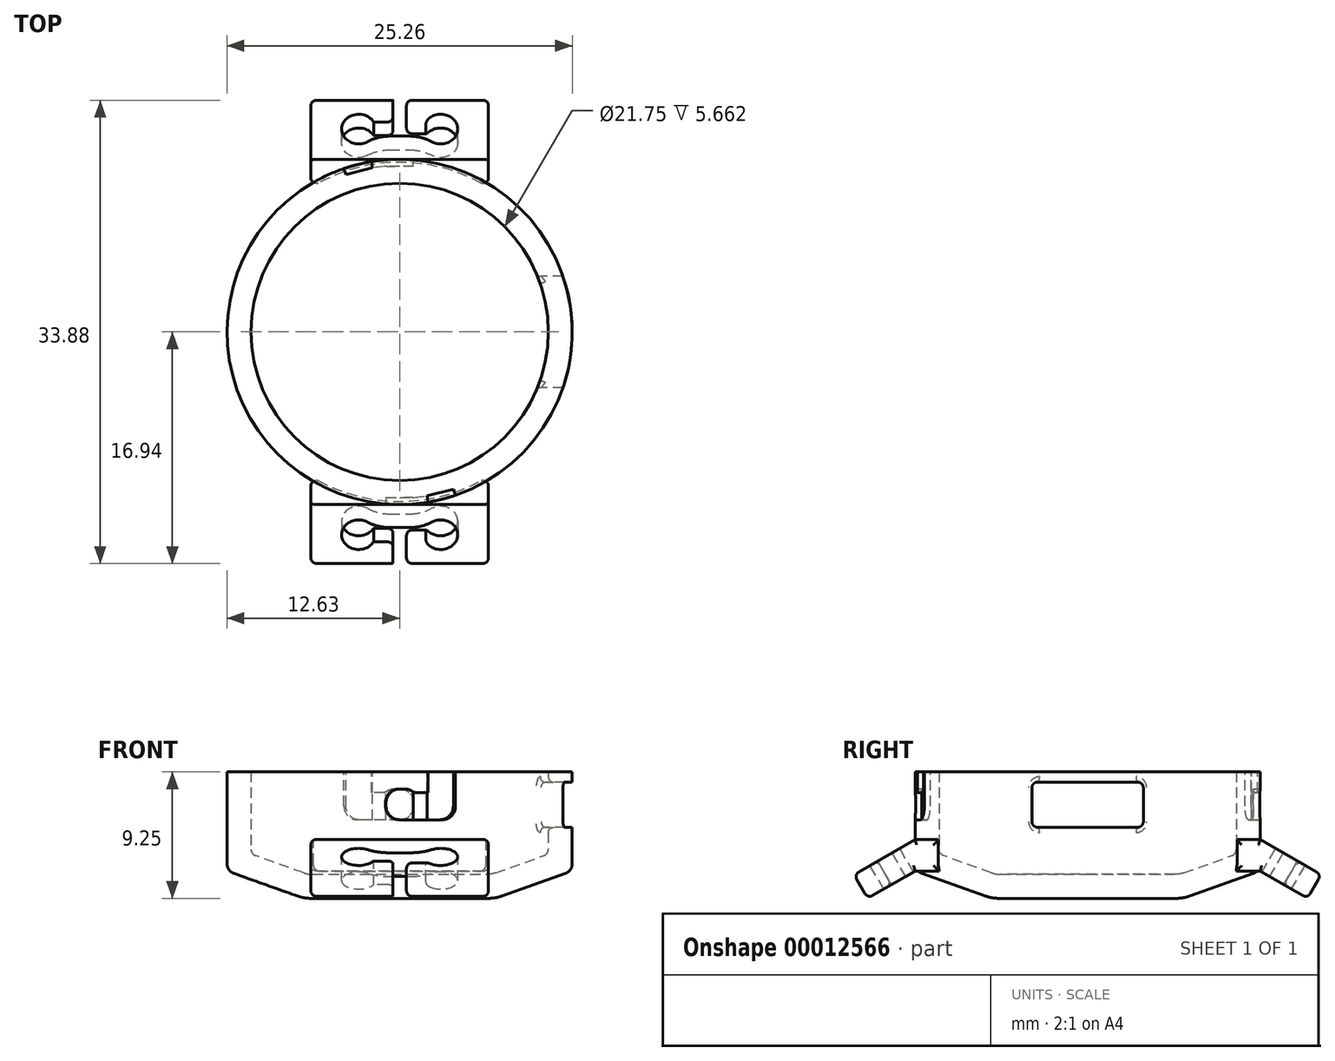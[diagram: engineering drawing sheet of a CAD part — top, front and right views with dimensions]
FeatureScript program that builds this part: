
annotation { "Feature Type Name" : "Feature", "Feature Type Description" : "" }
export const myFeature = defineFeature(function(context is Context, id is Id, definition is map)
    precondition{}
    {
        {
            var Q0;
            Q0=qCreatedBy(makeId("Front.planeOp"),FACE);
            var sketch = newSketch(context, id + "F0", { "sketchPlane" : qUnion([Q0])});
            skLineSegment(sketch, "E0", {"start": v(-12.62, 7.25) * mm, "end": v(-12.62, 0.53) * mm});
            skLineSegment(sketch, "E1", {"start": v(-12.13, -0.18) * mm, "end": v(-7.49, -1.83) * mm});
            skLineSegment(sketch, "E2", {"start": v(-6.48, -2) * mm, "end": v(0, -2) * mm});
            skLineSegment(sketch, "E3", {"start": v(0, -2) * mm, "end": v(0, -0.25) * mm});
            skLineSegment(sketch, "E4", {"start": v(0, -0.25) * mm, "end": v(-6.35, -0.25) * mm});
            skLineSegment(sketch, "E5", {"start": v(-7.02, -0.13) * mm, "end": v(-10.54, 1.12) * mm});
            skLineSegment(sketch, "E6", {"start": v(-10.88, 7.25) * mm, "end": v(-12.62, 7.25) * mm});
            skLineSegment(sketch, "E7", {"start": v(-10.88, 7.25) * mm, "end": v(-10.88, 1.59) * mm});
            skPoint(sketch, "E8.visualSharp", {"position": v(-12.62, 0) * mm});
            skArc(sketch, "E8.filletArc", {"start": v(-12.62, 0.53) * mm, "mid": v(-12.49, 0.1) * mm, "end": v(-12.13, -0.18) * mm});
            skPoint(sketch, "E9.visualSharp", {"position": v(-7, -2) * mm});
            skArc(sketch, "E9.filletArc", {"start": v(-7.49, -1.83) * mm, "mid": v(-7, -1.96) * mm, "end": v(-6.48, -2) * mm});
            skPoint(sketch, "E10.visualSharp", {"position": v(-10.88, 1.24) * mm});
            skArc(sketch, "E10.filletArc", {"start": v(-10.88, 1.59) * mm, "mid": v(-10.78, 1.3) * mm, "end": v(-10.54, 1.12) * mm});
            skPoint(sketch, "E11.visualSharp", {"position": v(-6.7, -0.25) * mm});
            skArc(sketch, "E11.filletArc", {"start": v(-7.02, -0.13) * mm, "mid": v(-6.7, -0.22) * mm, "end": v(-6.35, -0.25) * mm});
            skSolve(sketch);
        }
        {
            var Q0;
            Q0=makeQuery(id+"F0.imprint","IMPRINT",FACE,{"disambiguationData":[TD([[makeQuery(id+"F0.imprint","IMPRINT",EDGE,{"derivedFrom":sQuery(id+"F0.wireOp",EDGE,"E0")}),1.0]])]});
            var Q1;
            Q1=sQuery(id+"F0.wireOp",EDGE,"E3");
            revolve(context, id + "F1", {"entities" : qUnion([Q0]), "axis" : qUnion([Q1]), "revolveType" : RevolveType.FULL});
        }
        {
            var Q0;
            Q0=qCreatedBy(makeId("Right.planeOp"),FACE);
            var sketch = newSketch(context, id + "F2", { "sketchPlane" : qUnion([Q0])});
            skLineSegment(sketch, "E12", {"start": v(-10.88, 0) * mm, "end": v(-10.88, 2.3) * mm});
            skLineSegment(sketch, "E13", {"start": v(-10.88, 2.3) * mm, "end": v(-12.62, 2.3) * mm});
            skLineSegment(sketch, "E14", {"start": v(-12.62, 2.3) * mm, "end": v(-17.09, -0.27) * mm});
            skLineSegment(sketch, "E15", {"start": v(-17.09, -0.27) * mm, "end": v(-16.09, -2) * mm});
            skLineSegment(sketch, "E16", {"start": v(-16.09, -2) * mm, "end": v(-12.62, 0) * mm});
            skLineSegment(sketch, "E17", {"start": v(-12.62, 0) * mm, "end": v(-10.88, 0) * mm});
            skSolve(sketch);
        }
        {
            var Q0;
            Q0=makeQuery(id+"F2.imprint","IMPRINT",FACE,{"disambiguationData":[TD([[makeQuery(id+"F2.imprint","IMPRINT",EDGE,{"derivedFrom":sQuery(id+"F2.wireOp",EDGE,"E12")}),1.0]])]});
            extrude(context, id + "F3", {"entities" : qUnion([Q0]), "operationType" : NewBodyOperationType.ADD, "depth" : 6.5 * mm, "hasSecondDirection" : true, "secondDirectionOppositeDirection" : true, "secondDirectionDepth" : 6.5 * mm});
        }
        {
            var Q0;
            Q0=makeQuery(id+"F3.opExtrude","SWEPT_FACE",FACE,{"disambiguationData":[OSD([sQuery(id+"F2.wireOp",EDGE,"E14")])]});
            var sketch = newSketch(context, id + "F4", { "sketchPlane" : qUnion([Q0])});
            skLineSegment(sketch, "E18", {"start": v(-0.5, -14.93) * mm, "end": v(0.5, -14.93) * mm});
            skLineSegment(sketch, "E19", {"start": v(0.5, -14.93) * mm, "end": v(0.5, -12.93) * mm});
            skLineSegment(sketch, "E20", {"start": v(0.5, -12.93) * mm, "end": v(3, -12.93) * mm});
            skLineSegment(sketch, "E21", {"start": v(3, -12.93) * mm, "end": v(3, -11.73) * mm});
            skLineSegment(sketch, "E22", {"start": v(3, -11.73) * mm, "end": v(-3, -11.73) * mm});
            skLineSegment(sketch, "E23", {"start": v(-3, -11.73) * mm, "end": v(-3, -12.93) * mm});
            skLineSegment(sketch, "E24", {"start": v(-3, -12.93) * mm, "end": v(-0.5, -12.93) * mm});
            skLineSegment(sketch, "E25", {"start": v(-0.5, -12.93) * mm, "end": v(-0.5, -14.93) * mm});
            skCircle(sketch, "E26", {"center": v(-3, -12.33) * mm, "radius": 1.25 * mm});
            skCircle(sketch, "E27", {"center": v(3, -12.33) * mm, "radius": 1.25 * mm});
            skSolve(sketch);
        }
        {
            var Q0;
            {var subQ5=sQuery(id+"F4.wireOp",EDGE,"E23");Q0=makeQuery(id+"F4.imprint","IMPRINT",FACE,{"disambiguationData":[TD([[makeQuery(id+"F4.imprint","IMPRINT",EDGE,{"derivedFrom":subQ5}),-1.0]])]});}
            var Q1;
            {var subQ5=sQuery(id+"F4.wireOp",EDGE,"E23");Q1=makeQuery(id+"F4.imprint","IMPRINT",FACE,{"disambiguationData":[TD([[makeQuery(id+"F4.imprint","IMPRINT",EDGE,{"derivedFrom":subQ5}),1.0]])]});}
            var Q2;
            Q2=makeQuery(id+"F4.imprint","IMPRINT",FACE,{"disambiguationData":[TD([[makeQuery(id+"F4.imprint","IMPRINT",EDGE,{"derivedFrom":sQuery(id+"F4.wireOp",EDGE,"E18")}),-1.0]])]});
            var Q3;
            {var subQ5=sQuery(id+"F4.wireOp",EDGE,"E21");Q3=makeQuery(id+"F4.imprint","IMPRINT",FACE,{"disambiguationData":[TD([[makeQuery(id+"F4.imprint","IMPRINT",EDGE,{"derivedFrom":subQ5}),1.0]])]});}
            var Q4;
            {var subQ5=sQuery(id+"F4.wireOp",EDGE,"E21");Q4=makeQuery(id+"F4.imprint","IMPRINT",FACE,{"disambiguationData":[TD([[makeQuery(id+"F4.imprint","IMPRINT",EDGE,{"derivedFrom":subQ5}),-1.0]])]});}
            extrude(context, id + "F5", {"entities" : qUnion([Q0, Q1, Q2, Q3, Q4]), "operationType" : NewBodyOperationType.REMOVE, "endBound" : BoundingType.UP_TO_NEXT, "oppositeDirection" : true, "depth" : 25 * mm});
        }
        {
            var Q0;
            Q0=makeQuery(id+"F5.boolean.opBoolean","COPY",EDGE,{"derivedFrom":makeQuery(id+"F5.opExtrude","SWEPT_EDGE",EDGE,{"disambiguationData":[OSD([sQuery(id+"F4.wireOp",EDGE,"E22"),sQuery(id+"F4.wireOp",EDGE,"E26")])]})});
            var Q1;
            Q1=makeQuery(id+"F5.boolean.opBoolean","COPY",EDGE,{"derivedFrom":makeQuery(id+"F5.opExtrude","SWEPT_EDGE",EDGE,{"disambiguationData":[OSD([sQuery(id+"F4.wireOp",EDGE,"E22"),sQuery(id+"F4.wireOp",EDGE,"E27")])]})});
            fillet(context, id + "F6", {"entities" : qUnion([Q0, Q1]), "radius" : 3 * mm, "tangentPropagation" : true, "allowEdgeOverflow" : false});
        }
        {
            var Q0;
            Q0=makeQuery(id+"F5.boolean.opBoolean","COPY",EDGE,{"derivedFrom":makeQuery(id+"F5.opExtrude","SWEPT_EDGE",EDGE,{"disambiguationData":[OSD([sQuery(id+"F2.wireOp",EDGE,"E14"),sQuery(id+"F2.wireOp",EDGE,"E15"),sQuery(id+"F4.wireOp",EDGE,"E18"),sQuery(id+"F4.wireOp",EDGE,"E25")])]})});
            var Q1;
            Q1=makeQuery(id+"F5.boolean.opBoolean","COPY",EDGE,{"derivedFrom":makeQuery(id+"F5.opExtrude","SWEPT_EDGE",EDGE,{"disambiguationData":[OSD([sQuery(id+"F2.wireOp",EDGE,"E14"),sQuery(id+"F2.wireOp",EDGE,"E15"),sQuery(id+"F4.wireOp",EDGE,"E18"),sQuery(id+"F4.wireOp",EDGE,"E19")])]})});
            var Q2;
            Q2=makeQuery(id+"F5.boolean.opBoolean","COPY",EDGE,{"derivedFrom":makeQuery(id+"F5.opExtrude","SWEPT_EDGE",EDGE,{"disambiguationData":[OSD([sQuery(id+"F4.wireOp",EDGE,"E24"),sQuery(id+"F4.wireOp",EDGE,"E25")])]})});
            var Q3;
            Q3=makeQuery(id+"F5.boolean.opBoolean","COPY",EDGE,{"derivedFrom":makeQuery(id+"F5.opExtrude","SWEPT_EDGE",EDGE,{"disambiguationData":[OSD([sQuery(id+"F4.wireOp",EDGE,"E19"),sQuery(id+"F4.wireOp",EDGE,"E20")])]})});
            fillet(context, id + "F7", {"entities" : qUnion([Q0, Q1, Q2, Q3]), "radius" : .4 * mm, "tangentPropagation" : true, "allowEdgeOverflow" : false});
        }
        {
            var Q0;
            Q0=makeQuery(id+"F3.opExtrude","CAP_EDGE",EDGE,{"disambiguationData":[OSD([sQuery(id+"F2.wireOp",EDGE,"E13")])],"isStart":true});
            var Q1;
            Q1=makeQuery(id+"F3.opExtrude","CAP_EDGE",EDGE,{"disambiguationData":[OSD([sQuery(id+"F2.wireOp",EDGE,"E14")])],"isStart":true});
            var Q2;
            {var subQ0=sQuery(id+"F2.wireOp",EDGE,"E15");var subQ1=sQuery(id+"F2.wireOp",EDGE,"E14");Q2=makeQuery(id+"F5.boolean.opBoolean","SPLIT",EDGE,{"disambiguationData":[TD([makeQuery(id+"F5.opExtrude","SWEPT_FACE",FACE,{"disambiguationData":[OSD([sQuery(id+"F4.wireOp",EDGE,"E25")])]})])],"derivedFrom":makeQuery(id+"F3.opExtrude","SWEPT_EDGE",EDGE,{"disambiguationData":[OSD([subQ1,subQ0])]})});}
            var Q3;
            {var subQ0=sQuery(id+"F2.wireOp",EDGE,"E15");var subQ1=sQuery(id+"F2.wireOp",EDGE,"E14");Q3=makeQuery(id+"F5.boolean.opBoolean","SPLIT",EDGE,{"disambiguationData":[TD([makeQuery(id+"F5.opExtrude","SWEPT_FACE",FACE,{"disambiguationData":[OSD([sQuery(id+"F4.wireOp",EDGE,"E19")])]})])],"derivedFrom":makeQuery(id+"F3.opExtrude","SWEPT_EDGE",EDGE,{"disambiguationData":[OSD([subQ1,subQ0])]})});}
            var Q4;
            Q4=makeQuery(id+"F5.boolean.opBoolean","COPY",EDGE,{"derivedFrom":makeQuery(id+"F5.opExtrude","CAP_EDGE",EDGE,{"disambiguationData":[OSD([sQuery(id+"F4.wireOp",EDGE,"E27")])],"isStart":true})});
            var Q5;
            Q5=makeQuery(id+"F3.opExtrude","CAP_EDGE",EDGE,{"disambiguationData":[OSD([sQuery(id+"F2.wireOp",EDGE,"E14")])],"isStart":false});
            var Q6;
            Q6=makeQuery(id+"F3.opExtrude","CAP_EDGE",EDGE,{"disambiguationData":[OSD([sQuery(id+"F2.wireOp",EDGE,"E13")])],"isStart":false});
            var Q7;
            Q7=makeQuery(id+"F3.opExtrude","CAP_EDGE",EDGE,{"disambiguationData":[OSD([sQuery(id+"F2.wireOp",EDGE,"E12")])],"isStart":false});
            var Q8;
            Q8=makeQuery(id+"F3.opExtrude","CAP_EDGE",EDGE,{"disambiguationData":[OSD([sQuery(id+"F2.wireOp",EDGE,"E17")])],"isStart":false});
            var Q9;
            Q9=makeQuery(id+"F3.opExtrude","CAP_EDGE",EDGE,{"disambiguationData":[OSD([sQuery(id+"F2.wireOp",EDGE,"E16")])],"isStart":false});
            var Q10;
            Q10=makeQuery(id+"F3.opExtrude","CAP_EDGE",EDGE,{"disambiguationData":[OSD([sQuery(id+"F2.wireOp",EDGE,"E15")])],"isStart":false});
            var Q11;
            {var subQ0=sQuery(id+"F2.wireOp",EDGE,"E16");var subQ1=sQuery(id+"F2.wireOp",EDGE,"E15");Q11=makeQuery(id+"F5.boolean.opBoolean","SPLIT",EDGE,{"disambiguationData":[TD([makeQuery(id+"F5.opExtrude","SWEPT_FACE",FACE,{"disambiguationData":[OSD([sQuery(id+"F4.wireOp",EDGE,"E19")])]})])],"derivedFrom":makeQuery(id+"F3.opExtrude","SWEPT_EDGE",EDGE,{"disambiguationData":[OSD([subQ1,subQ0])]})});}
            var Q12;
            {var subQ0=sQuery(id+"F2.wireOp",EDGE,"E16");var subQ1=sQuery(id+"F2.wireOp",EDGE,"E15");Q12=makeQuery(id+"F5.boolean.opBoolean","SPLIT",EDGE,{"disambiguationData":[TD([makeQuery(id+"F5.opExtrude","SWEPT_FACE",FACE,{"disambiguationData":[OSD([sQuery(id+"F4.wireOp",EDGE,"E25")])]})])],"derivedFrom":makeQuery(id+"F3.opExtrude","SWEPT_EDGE",EDGE,{"disambiguationData":[OSD([subQ1,subQ0])]})});}
            var Q13;
            Q13=makeQuery(id+"F5.boolean.opBoolean","COPY",EDGE,{"derivedFrom":makeQuery(id+"F5.opExtrude","CAP_EDGE",EDGE,{"disambiguationData":[OSD([sQuery(id+"F4.wireOp",EDGE,"E26")])],"isStart":false})});
            var Q14;
            Q14=makeQuery(id+"F3.opExtrude","CAP_EDGE",EDGE,{"disambiguationData":[OSD([sQuery(id+"F2.wireOp",EDGE,"E15")])],"isStart":true});
            var Q15;
            Q15=makeQuery(id+"F3.opExtrude","CAP_EDGE",EDGE,{"disambiguationData":[OSD([sQuery(id+"F2.wireOp",EDGE,"E16")])],"isStart":true});
            var Q16;
            Q16=makeQuery(id+"F3.opExtrude","CAP_EDGE",EDGE,{"disambiguationData":[OSD([sQuery(id+"F2.wireOp",EDGE,"E17")])],"isStart":true});
            var Q17;
            Q17=makeQuery(id+"F3.opExtrude","CAP_EDGE",EDGE,{"disambiguationData":[OSD([sQuery(id+"F2.wireOp",EDGE,"E12")])],"isStart":true});
            fillet(context, id + "F8", {"entities" : qUnion([Q0, Q1, Q2, Q3, Q4, Q5, Q6, Q7, Q8, Q9, Q10, Q11, Q12, Q13, Q14, Q15, Q16, Q17]), "radius" : .4 * mm, "tangentPropagation" : true, "allowEdgeOverflow" : false});
        }
        {
            var Q0;
            Q0=makeQuery(id+"F1.opRevolve","SWEPT_BODY",BODY,{"disambiguationData":[OSD([sQuery(id+"F0.wireOp",EDGE,"E0"),sQuery(id+"F0.wireOp",EDGE,"E1"),sQuery(id+"F0.wireOp",EDGE,"E2"),sQuery(id+"F0.wireOp",EDGE,"E3"),sQuery(id+"F0.wireOp",EDGE,"E4"),sQuery(id+"F0.wireOp",EDGE,"E5"),sQuery(id+"F0.wireOp",EDGE,"E6"),sQuery(id+"F0.wireOp",EDGE,"E7"),sQuery(id+"F0.wireOp",EDGE,"E8.filletArc"),sQuery(id+"F0.wireOp",EDGE,"E9.filletArc"),sQuery(id+"F0.wireOp",EDGE,"E10.filletArc"),sQuery(id+"F0.wireOp",EDGE,"E11.filletArc")])]});
            var Q1;
            Q1=qCreatedBy(makeId("Front.planeOp"),FACE);
            mirror(context, id + "F9", {"operationType" : NewBodyOperationType.ADD, "entities" : qUnion([Q0]), "mirrorPlane" : qUnion([Q1])});
        }
        {
            var Q0;
            Q0=qCreatedBy(makeId("Right.planeOp"),FACE);
            var sketch = newSketch(context, id + "F10", { "sketchPlane" : qUnion([Q0])});
            skLineSegment(sketch, "E28.bottom", {"start": v(-3.68, 6.5) * mm, "end": v(3.68, 6.5) * mm});
            skLineSegment(sketch, "E28.top", {"start": v(-3.68, 3.2) * mm, "end": v(3.68, 3.2) * mm});
            skLineSegment(sketch, "E28.left", {"start": v(-4.08, 6.1) * mm, "end": v(-4.08, 3.6) * mm});
            skLineSegment(sketch, "E28.right", {"start": v(4.08, 6.1) * mm, "end": v(4.08, 3.6) * mm});
            skPoint(sketch, "E29.visualSharp", {"position": v(-4.08, 6.5) * mm});
            skArc(sketch, "E29.filletArc", {"start": v(-3.68, 6.5) * mm, "mid": v(-3.96, 6.38) * mm, "end": v(-4.08, 6.1) * mm});
            skPoint(sketch, "E30.visualSharp", {"position": v(4.08, 6.5) * mm});
            skArc(sketch, "E30.filletArc", {"start": v(4.08, 6.1) * mm, "mid": v(3.96, 6.38) * mm, "end": v(3.68, 6.5) * mm});
            skPoint(sketch, "E31.visualSharp", {"position": v(4.08, 3.2) * mm});
            skArc(sketch, "E31.filletArc", {"start": v(3.68, 3.2) * mm, "mid": v(3.96, 3.32) * mm, "end": v(4.08, 3.6) * mm});
            skPoint(sketch, "E32.visualSharp", {"position": v(-4.08, 3.2) * mm});
            skArc(sketch, "E32.filletArc", {"start": v(-4.08, 3.6) * mm, "mid": v(-3.96, 3.32) * mm, "end": v(-3.68, 3.2) * mm});
            skSolve(sketch);
        }
        {
            var Q0;
            Q0 = qSketchRegion(id + "F10", true);
            var Q1;
            Q1=makeQuery(id+"F1.opRevolve","SWEPT_FACE",FACE,{"disambiguationData":[OSD([sQuery(id+"F0.wireOp",EDGE,"E0")])]});
            extrude(context, id + "F11", {"entities" : qUnion([Q0]), "operationType" : NewBodyOperationType.REMOVE, "endBound" : BoundingType.UP_TO_SURFACE, "endBoundEntityFace" : qUnion([Q1]), "depth" : 25 * mm});
        }
        {
            var Q0;
            Q0=makeQuery(id+"F11.boolean.opBoolean","COPY",EDGE,{"derivedFrom":makeQuery(id+"F11.opExtrude","CAP_EDGE",EDGE,{"disambiguationData":[OSD([sQuery(id+"F10.wireOp",EDGE,"E28.bottom")])],"isStart":false})});
            var Q1;
            Q1=makeQuery(id+"F11.boolean.opBoolean","INTERSECT",EDGE,{"derivedFrom":[makeQuery(id+"F1.opRevolve","SWEPT_FACE",FACE,{"disambiguationData":[OSD([sQuery(id+"F0.wireOp",EDGE,"E7")])]}),makeQuery(id+"F11.opExtrude","SWEPT_FACE",FACE,{"disambiguationData":[OSD([sQuery(id+"F10.wireOp",EDGE,"E28.top")])]})]});
            fillet(context, id + "F12", {"entities" : qUnion([Q0, Q1]), "radius" : .4 * mm, "tangentPropagation" : true, "allowEdgeOverflow" : false});
        }
        {
            var Q0;
            Q0=makeQuery(id+"F1.opRevolve","SWEPT_FACE",FACE,{"disambiguationData":[OSD([sQuery(id+"F0.wireOp",EDGE,"E6")])]});
            cPlane(context, id + "F13", {"entities" : qUnion([Q0]), "cplaneType" : CPlaneType.OFFSET, "offset" : 1.5 * mm, "oppositeDirection" : true, "width" : 150 * mm, "height" : 150 * mm});
        }
        {
            var Q0;
            Q0=qCreatedBy(id+"F13.planeOp",FACE);
            var sketch = newSketch(context, id + "F14", { "sketchPlane" : qUnion([Q0])});
            skLineSegment(sketch, "E33", {"start": v(0, 0) * mm, "end": v(0, -12.62) * mm, "construction": true});
            skCircle(sketch, "E34", {"center": v(0, 0) * mm, "radius": 12.62 * mm});
            skLineSegment(sketch, "E35", {"start": v(-1, -12.12) * mm, "end": v(1, -12.12) * mm});
            skLineSegment(sketch, "E36", {"start": v(0, 0) * mm, "end": v(-1.04, -12.58) * mm});
            skLineSegment(sketch, "E37", {"start": v(0, 0) * mm, "end": v(1.04, -12.58) * mm});
            skLineSegment(sketch, "E38", {"start": v(1, -12.12) * mm, "end": v(2, -12) * mm});
            skLineSegment(sketch, "E39", {"start": v(0, 0) * mm, "end": v(2.07, -12.45) * mm});
            skLineSegment(sketch, "E40", {"start": v(0, 0) * mm, "end": v(1.5, -12.06) * mm, "construction": true});
            skLineSegment(sketch, "E41", {"start": v(2, -12) * mm, "end": v(3.93, -11.51) * mm});
            skLineSegment(sketch, "E42", {"start": v(0, 0) * mm, "end": v(4.08, -11.95) * mm});
            skLineSegment(sketch, "E43", {"start": v(0, 0) * mm, "end": v(2.96, -11.76) * mm, "construction": true});
            skLineSegment(sketch, "E44.1.0", {"start": v(0, 0) * mm, "end": v(-4.08, 11.95) * mm});
            skLineSegment(sketch, "E44.1.1", {"start": v(-2, 12) * mm, "end": v(-3.93, 11.51) * mm});
            skLineSegment(sketch, "E44.1.2", {"start": v(0, 0) * mm, "end": v(-2.07, 12.45) * mm});
            skLineSegment(sketch, "E44.1.3", {"start": v(-1, 12.12) * mm, "end": v(-2, 12) * mm});
            skLineSegment(sketch, "E44.1.4", {"start": v(0, 0) * mm, "end": v(-1.04, 12.58) * mm});
            skLineSegment(sketch, "E44.1.5", {"start": v(1, 12.13) * mm, "end": v(-1, 12.13) * mm});
            skLineSegment(sketch, "E44.1.6", {"start": v(0, 0) * mm, "end": v(1.04, 12.58) * mm});
            skLineSegment(sketch, "E44.anchor1", {"start": v(0, 0) * mm, "end": v(4.08, -11.95) * mm, "construction": true});
            skLineSegment(sketch, "E44.anchor2", {"start": v(0, 0) * mm, "end": v(-4.08, 11.95) * mm, "construction": true});
            skSolve(sketch);
        }
        {
            var Q0;
            {var subQ3=sQuery(id+"F14.wireOp",EDGE,"E35");Q0=makeQuery(id+"F14.imprint","IMPRINT",FACE,{"disambiguationData":[TD([[makeQuery(id+"F14.imprint","IMPRINT",EDGE,{"derivedFrom":subQ3}),-1.0]])]});}
            var Q1;
            {var subQ3=sQuery(id+"F14.wireOp",EDGE,"E44.1.5");Q1=makeQuery(id+"F14.imprint","IMPRINT",FACE,{"disambiguationData":[TD([[makeQuery(id+"F14.imprint","IMPRINT",EDGE,{"derivedFrom":subQ3}),-1.0]])]});}
            extrude(context, id + "F15", {"entities" : qUnion([Q0, Q1]), "operationType" : NewBodyOperationType.REMOVE, "oppositeDirection" : true, "depth" : 2 * mm, "hasSecondDirection" : true, "secondDirectionOppositeDirection" : false, "secondDirectionDepth" : .25 * mm});
        }
        {
            var Q0;
            {var subQ3=sQuery(id+"F14.wireOp",EDGE,"E38");Q0=makeQuery(id+"F14.imprint","IMPRINT",FACE,{"disambiguationData":[TD([[makeQuery(id+"F14.imprint","IMPRINT",EDGE,{"derivedFrom":subQ3}),-1.0]])]});}
            var Q1;
            {var subQ3=sQuery(id+"F14.wireOp",EDGE,"E44.1.3");Q1=makeQuery(id+"F14.imprint","IMPRINT",FACE,{"disambiguationData":[TD([[makeQuery(id+"F14.imprint","IMPRINT",EDGE,{"derivedFrom":subQ3}),-1.0]])]});}
            extrude(context, id + "F16", {"entities" : qUnion([Q0, Q1]), "operationType" : NewBodyOperationType.REMOVE, "oppositeDirection" : true, "depth" : 2 * mm});
        }
        {
            var Q0;
            {var subQ3=sQuery(id+"F14.wireOp",EDGE,"E41");Q0=makeQuery(id+"F14.imprint","IMPRINT",FACE,{"disambiguationData":[TD([[makeQuery(id+"F14.imprint","IMPRINT",EDGE,{"derivedFrom":subQ3}),-1.0]])]});}
            var Q1;
            {var subQ3=sQuery(id+"F14.wireOp",EDGE,"E44.1.1");Q1=makeQuery(id+"F14.imprint","IMPRINT",FACE,{"disambiguationData":[TD([[makeQuery(id+"F14.imprint","IMPRINT",EDGE,{"derivedFrom":subQ3}),-1.0]])]});}
            extrude(context, id + "F17", {"entities" : qUnion([Q0, Q1]), "operationType" : NewBodyOperationType.REMOVE, "oppositeDirection" : true, "depth" : 2 * mm, "hasSecondDirection" : true, "secondDirectionBound" : SecondDirectionBoundingType.UP_TO_NEXT, "secondDirectionOppositeDirection" : false, "secondDirectionDepth" : 25 * mm});
        }
        {
            var Q0;
            Q0=makeQuery(id+"F15.boolean.opBoolean","COPY",EDGE,{"derivedFrom":makeQuery(id+"F15.opExtrude","CAP_EDGE",EDGE,{"disambiguationData":[OSD([sQuery(id+"F14.wireOp",EDGE,"E37")])],"isStart":true})});
            var Q1;
            Q1=makeQuery(id+"F15.boolean.opBoolean","COPY",EDGE,{"derivedFrom":makeQuery(id+"F15.opExtrude","CAP_EDGE",EDGE,{"disambiguationData":[OSD([sQuery(id+"F14.wireOp",EDGE,"E36")])],"isStart":true})});
            var Q2;
            Q2=makeQuery(id+"F15.boolean.opBoolean","COPY",EDGE,{"derivedFrom":makeQuery(id+"F15.opExtrude","CAP_EDGE",EDGE,{"disambiguationData":[OSD([sQuery(id+"F14.wireOp",EDGE,"E36")])],"isStart":false})});
            var Q3;
            Q3=makeQuery(id+"F17.boolean.opBoolean","COPY",EDGE,{"derivedFrom":makeQuery(id+"F17.opExtrude","CAP_EDGE",EDGE,{"disambiguationData":[OSD([sQuery(id+"F14.wireOp",EDGE,"E42")])],"isStart":false})});
            var Q4;
            Q4=makeQuery(id+"F15.boolean.opBoolean","COPY",EDGE,{"derivedFrom":makeQuery(id+"F15.opExtrude","CAP_EDGE",EDGE,{"disambiguationData":[OSD([sQuery(id+"F14.wireOp",EDGE,"E44.1.4")])],"isStart":true})});
            var Q5;
            Q5=makeQuery(id+"F15.boolean.opBoolean","COPY",EDGE,{"derivedFrom":makeQuery(id+"F15.opExtrude","CAP_EDGE",EDGE,{"disambiguationData":[OSD([sQuery(id+"F14.wireOp",EDGE,"E44.1.6")])],"isStart":true})});
            var Q6;
            Q6=makeQuery(id+"F15.boolean.opBoolean","COPY",EDGE,{"derivedFrom":makeQuery(id+"F15.opExtrude","CAP_EDGE",EDGE,{"disambiguationData":[OSD([sQuery(id+"F14.wireOp",EDGE,"E44.1.6")])],"isStart":false})});
            var Q7;
            Q7=makeQuery(id+"F17.boolean.opBoolean","COPY",EDGE,{"derivedFrom":makeQuery(id+"F17.opExtrude","CAP_EDGE",EDGE,{"disambiguationData":[OSD([sQuery(id+"F14.wireOp",EDGE,"E44.1.0")])],"isStart":false})});
            fillet(context, id + "F18", {"entities" : qUnion([Q0, Q1, Q2, Q3, Q4, Q5, Q6, Q7]), "radius" : 1 * mm, "tangentPropagation" : true, "allowEdgeOverflow" : false});
        }
        {
            var Q0;
            Q0=makeQuery(id+"F16.boolean.opBoolean","COPY",EDGE,{"derivedFrom":makeQuery(id+"F16.opExtrude","CAP_EDGE",EDGE,{"disambiguationData":[OSD([sQuery(id+"F14.wireOp",EDGE,"E37")])],"isStart":true})});
            var Q1;
            Q1=makeQuery(id+"F16.boolean.opBoolean","COPY",EDGE,{"derivedFrom":makeQuery(id+"F16.opExtrude","CAP_EDGE",EDGE,{"disambiguationData":[OSD([sQuery(id+"F14.wireOp",EDGE,"E39")])],"isStart":true})});
            var Q2;
            Q2=makeQuery(id+"F16.boolean.opBoolean","COPY",EDGE,{"derivedFrom":makeQuery(id+"F16.opExtrude","CAP_EDGE",EDGE,{"disambiguationData":[OSD([sQuery(id+"F14.wireOp",EDGE,"E44.1.2")])],"isStart":true})});
            var Q3;
            Q3=makeQuery(id+"F16.boolean.opBoolean","COPY",EDGE,{"derivedFrom":makeQuery(id+"F16.opExtrude","CAP_EDGE",EDGE,{"disambiguationData":[OSD([sQuery(id+"F14.wireOp",EDGE,"E44.1.4")])],"isStart":true})});
            var Q4;
            {var subQ0=sQuery(id+"F14.wireOp",EDGE,"E37");Q4=makeQuery(id+"F18.opFillet","BLEND_EDGE",EDGE,{"blendedFrom":[makeQuery(id+"F15.boolean.opBoolean","COPY",EDGE,{"derivedFrom":makeQuery(id+"F15.opExtrude","CAP_EDGE",EDGE,{"disambiguationData":[OSD([subQ0])],"isStart":true})}),makeQuery(id+"F16.boolean.opBoolean","COPY",FACE,{"derivedFrom":makeQuery(id+"F16.opExtrude","CAP_FACE",FACE,{"disambiguationData":[OSD([sQuery(id+"F14.wireOp",EDGE,"E34"),subQ0,sQuery(id+"F14.wireOp",EDGE,"E38"),sQuery(id+"F14.wireOp",EDGE,"E39")])],"isStart":true})})],"blendedInto":[makeQuery(id+"F16.boolean.opBoolean","COPY",FACE,{"derivedFrom":makeQuery(id+"F16.opExtrude","CAP_FACE",FACE,{"disambiguationData":[OSD([sQuery(id+"F14.wireOp",EDGE,"E34"),subQ0,sQuery(id+"F14.wireOp",EDGE,"E38"),sQuery(id+"F14.wireOp",EDGE,"E39")])],"isStart":true})})]});}
            var Q5;
            {var subQ0=sQuery(id+"F14.wireOp",EDGE,"E44.1.4");Q5=makeQuery(id+"F18.opFillet","BLEND_EDGE",EDGE,{"blendedFrom":[makeQuery(id+"F15.boolean.opBoolean","COPY",EDGE,{"derivedFrom":makeQuery(id+"F15.opExtrude","CAP_EDGE",EDGE,{"disambiguationData":[OSD([subQ0])],"isStart":true})}),makeQuery(id+"F16.boolean.opBoolean","COPY",FACE,{"derivedFrom":makeQuery(id+"F16.opExtrude","CAP_FACE",FACE,{"disambiguationData":[OSD([sQuery(id+"F14.wireOp",EDGE,"E34"),sQuery(id+"F14.wireOp",EDGE,"E44.1.2"),sQuery(id+"F14.wireOp",EDGE,"E44.1.3"),subQ0])],"isStart":true})})],"blendedInto":[makeQuery(id+"F16.boolean.opBoolean","COPY",FACE,{"derivedFrom":makeQuery(id+"F16.opExtrude","CAP_FACE",FACE,{"disambiguationData":[OSD([sQuery(id+"F14.wireOp",EDGE,"E34"),sQuery(id+"F14.wireOp",EDGE,"E44.1.2"),sQuery(id+"F14.wireOp",EDGE,"E44.1.3"),subQ0])],"isStart":true})})]});}
            fillet(context, id + "F19", {"entities" : qUnion([Q0, Q1, Q2, Q3, Q4, Q5]), "radius" : .25 * mm, "tangentPropagation" : true, "allowEdgeOverflow" : false});
        }
    });
